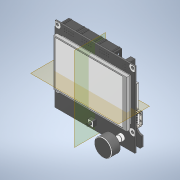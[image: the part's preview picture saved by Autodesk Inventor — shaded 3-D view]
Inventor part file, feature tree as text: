
AUTODESK INVENTOR PART (.ipt)
format: ipt  version: 2022 (Build 260153000, 153)  size: 5,202,944 bytes
history: native  units: in
note: dims shown in document units (in); Inventor stores cm internally (conversion verified against a paired STEP export)
features: other x55, plane x2
ambient origin geometry x8: Origin, YZ Plane, XZ Plane, XY Plane, X Axis, Y Axis, Z Axis, Center Point
bodies: Solid1 (feature_tree), Solid2 (feature_tree), Solid3 (feature_tree), Solid4 (feature_tree), Solid5 (feature_tree), Solid6 (feature_tree), Solid7 (feature_tree), Solid8 (feature_tree), Solid9 (feature_tree), Solid10 (feature_tree), Solid11 (feature_tree), Solid12 (feature_tree), Solid13 (feature_tree), Solid14 (feature_tree), Solid15 (feature_tree), Solid16 (feature_tree), Solid17 (feature_tree), Solid18 (feature_tree), Solid19 (feature_tree), Solid20 (feature_tree), Solid21 (feature_tree), Solid22 (feature_tree), Solid23 (feature_tree), Solid24 (feature_tree), Solid25 (feature_tree), Solid26 (feature_tree), Solid27 (feature_tree), Solid28 (feature_tree), Solid29 (feature_tree), Solid30 (feature_tree), Solid31 (feature_tree), Solid32 (feature_tree), Solid33 (feature_tree), Solid34 (feature_tree), Solid35 (feature_tree), Solid36 (feature_tree), Solid37 (feature_tree), Solid38 (feature_tree), Solid39 (feature_tree), Solid40 (feature_tree), Solid41 (feature_tree), Solid42 (feature_tree), Solid43 (feature_tree), Solid44 (feature_tree), Solid45 (feature_tree), Solid46 (feature_tree), Solid47 (feature_tree), Solid48 (feature_tree), Solid49 (feature_tree), Solid50 (feature_tree), Solid51 (feature_tree), Solid52 (feature_tree), Solid53 (feature_tree), Solid54 (feature_tree), Solid55 (feature_tree), Solid56 (feature_tree)
feature tree (57):
  plane  "Work Plane1"
  plane  "Work Plane2"
  other  "PCB_1:1"
  other  "Reset_1_Reset_Corpo1_1:1"
  other  "cap_1_cap_Corpo1_1:1"
  other  "TFT Display_1:1"
  other  "Straight Contact_13_Straight Contact_Corpo1_1:1"
  other  "Straight Contact_6_Straight Contact_Corpo1_1:1"
  other  "Straight Contact_5_Straight Contact_Corpo1_1:1"
  other  "Straight Contact_12_Straight Contact_Corpo1_1:1"
  other  "Straight Contact_11_Straight Contact_Corpo1_1:1"
  other  "Straight Contact_4_Straight Contact_Corpo1_1:1"
  other  "Straight Contact_3_Straight Contact_Corpo1_1:1"
  other  "Straight Contact_10_Straight Contact_Corpo1_1:1"
  other  "Straight Contact_9_Straight Contact_Corpo1_1:1"
  other  "Straight Contact_2_Straight Contact_Corpo1_1:1"
  other  "14_Pin Shrouded Header Body_1_14_Pin Shrouded Header Body_Corpo1_1:1"
  other  "Straight Contact_13_Straight Contact_Corpo1 (1)_1:1"
  other  "Straight Contact_6_Straight Contact_Corpo1 (1)_1:1"
  other  "Straight Contact_5_Straight Contact_Corpo1 (1)_1:1"
  other  "Straight Contact_12_Straight Contact_Corpo1 (1)_1:1"
  other  "Straight Contact_11_Straight Contact_Corpo1 (1)_1:1"
  other  "Straight Contact_4_Straight Contact_Corpo1 (1)_1:1"
  other  "Straight Contact_3_Straight Contact_Corpo1 (1)_1:1"
  other  "Straight Contact_10_Straight Contact_Corpo1 (1)_1:1"
  other  "Straight Contact_9_Straight Contact_Corpo1 (1)_1:1"
  other  "Straight Contact_2_Straight Contact_Corpo1 (1)_1:1"
  other  "14_Pin Shrouded Header Body_1_14_Pin Shrouded Header Body_Corpo1 (1)_1:1"
  other  "Straight Contact_13_Straight Contact_Corpo1 (2)_1:1"
  other  "Straight Contact_6_Straight Contact_Corpo1 (2)_1:1"
  other  "Straight Contact_5_Straight Contact_Corpo1 (2)_1:1"
  other  "Straight Contact_12_Straight Contact_Corpo1 (2)_1:1"
  other  "Straight Contact_11_Straight Contact_Corpo1 (2)_1:1"
  other  "Straight Contact_4_Straight Contact_Corpo1 (2)_1:1"
  other  "Straight Contact_3_Straight Contact_Corpo1 (2)_1:1"
  other  "Straight Contact_10_Straight Contact_Corpo1 (2)_1:1"
  other  "Straight Contact_9_Straight Contact_Corpo1 (2)_1:1"
  other  "Straight Contact_2_Straight Contact_Corpo1 (2)_1:1"
  other  "14_Pin Shrouded Header Body_1_14_Pin Shrouded Header Body_Corpo1 (2)_1:1"
  other  "JST _ XH _ SMD _R_ _ 5Pin _ 2_54mm v1_2_JST _ XH _ SMD _R_ _ 5Pin _ 2_54mm_Corpo1_1:1"
  other  "JST _ XH _ SMD _R_ _ 5Pin _ 2_54mm v1_2_JST _ XH _ SMD _R_ _ 5Pin _ 2_54mm_Corpo1 (1)_1:1"
  other  "JST _ XH _ SMD _R_ _ 2Pin _ 2_54mm v2_1_JST _ XH _ SMD _R_ _ 2Pin _ 2_54mm_Corpo1_1:1"
  other  "JST _ XH _ SMD _R_ _ 3Pin _ 2_54mm v1_4_JST _ XH _ SMD _R_ _ 3Pin _ 2_54mm_Corpo1_1:1"
  other  "JST _ XH _ SMD _R_ _ 3Pin _ 2_54mm v1_4_JST _ XH _ SMD _R_ _ 3Pin _ 2_54mm_Corpo1 (1)_1:1"
  other  "JST _ XH _ SMD _R_ _ 3Pin _ 2_54mm v1_4_JST _ XH _ SMD _R_ _ 3Pin _ 2_54mm_Corpo1 (2)_1:1"
  other  "JST _ XH _ SMD _R_ _ 3Pin _ 2_54mm v1_4_JST _ XH _ SMD _R_ _ 3Pin _ 2_54mm_Corpo1 (3)_1:1"
  other  "Buzzer_1_Buzzer_Corpo1_1:1"
  other  "PBD_8 v3_1_PBD_8_Corpo1_1:1"
  other  "SD Slot_1_SD Slot_Corpo1_1:1"
  other  "Componente4_1_Componente4_Corpo1_1:1"
  other  "Componente3_1_Componente3_Corpo1_1:1"
  other  "Componente6_1_Componente6_Corpo1_1:1"
  other  "Componente7_1_Componente7_Corpo1_1:1"
  other  "Componente2_1_Componente2_Corpo1_1:1"
  other  "Componente8_1_Componente8_Corpo1_1:1"
  other  "Componente5_1_Componente5_Corpo1_1:1"
  other  "Componente9_1_Componente9_Corpo1_1:1"
